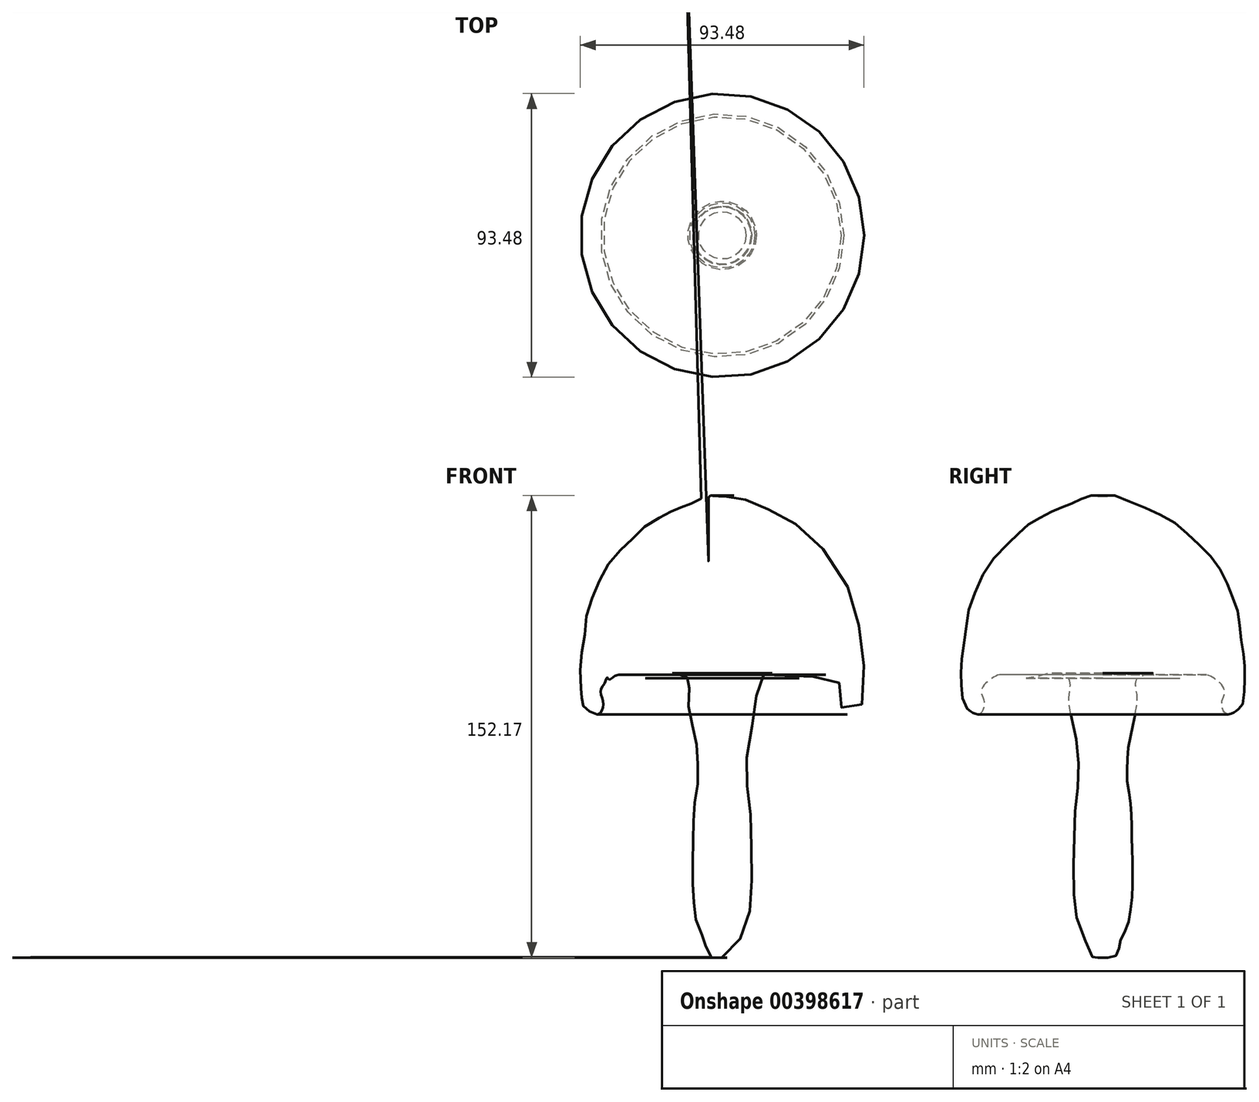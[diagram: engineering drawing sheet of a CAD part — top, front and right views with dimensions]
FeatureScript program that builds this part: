
annotation { "Feature Type Name" : "Feature", "Feature Type Description" : "" }
export const myFeature = defineFeature(function(context is Context, id is Id, definition is map)
    precondition{}
    {
        {
            var Q0;
            Q0=qCreatedBy(makeId("Front.planeOp"),FACE);
            var sketch = newSketch(context, id + "F0", { "sketchPlane" : qUnion([Q0])});
            skLineSegment(sketch, "E0", {"start": v(0, 76.27) * mm, "end": v(0, -75.74) * mm});
            skFitSpline(sketch, "E1", {"points": [v(0, 76.27) * mm, v(2.18, 76.27) * mm, v(4.95, 76.27) * mm, v(8.7, 74.48) * mm, v(11.48, 73.3) * mm, v(13.66, 72.5) * mm, v(17.22, 70.92) * mm, v(18.8, 70.13) * mm, v(25.53, 66.17) * mm, v(27.51, 64.2) * mm, v(36.42, 55.29) * mm, v(40.77, 47.57) * mm, v(44.53, 37.67) * mm, v(45.13, 32.33) * mm, v(46.51, 22.63) * mm, v(46.7, 16.9) * mm, v(46.11, 7.98) * mm, v(45.13, 6.4) * mm, v(40.77, 4.42) * mm, v(39.19, 8.38) * mm, v(39.98, 10.95) * mm, v(39.39, 13.72) * mm, v(35.03, 17.09) * mm, v(33.65, 17.29) * mm, v(28.5, 16.5) * mm, v(23.95, 16.3) * mm, v(20.58, 17.09) * mm, v(19, 17.68) * mm, v(15.44, 17.88) * mm, v(14.05, 17.48) * mm, v(11.28, 16.1) * mm, v(10.89, 12.73) * mm, v(11.28, 9.17) * mm, v(10.3, 3.04) * mm, v(9.7, 0) * mm, v(8.31, -6.66) * mm, v(8.11, -10.03) * mm, v(7.92, -13.59) * mm, v(7.92, -17.75) * mm, v(8.9, -22.9) * mm, v(9.1, -26.26) * mm, v(9.5, -31.2) * mm, v(9.5, -35.76) * mm, v(9.7, -42.09) * mm, v(9.7, -46.84) * mm, v(9.7, -53.57) * mm, v(9.3, -58.32) * mm, v(8.9, -61.68) * mm, v(7.72, -66.43) * mm, v(5.74, -70.2) * mm, v(4.55, -74.94) * mm, v(0, -75.74) * mm], "startDerivative": vector(153.57, -5.92) * mm, "endDerivative": vector(-274.16, 14.34) * mm});
            skSolve(sketch);
        }
        {
            var Q0;
            Q0=makeQuery(id+"F0.imprint","IMPRINT",FACE,{"disambiguationData":[TD([[makeQuery(id+"F0.imprint","IMPRINT",EDGE,{"derivedFrom":sQuery(id+"F0.wireOp",EDGE,"E0")}),1.0]])]});
            var Q1;
            Q1=sQuery(id+"F0.wireOp",EDGE,"E0");
            revolve(context, id + "F1", {"entities" : qUnion([Q0]), "axis" : qUnion([Q1]), "revolveType" : RevolveType.FULL});
        }
    });
